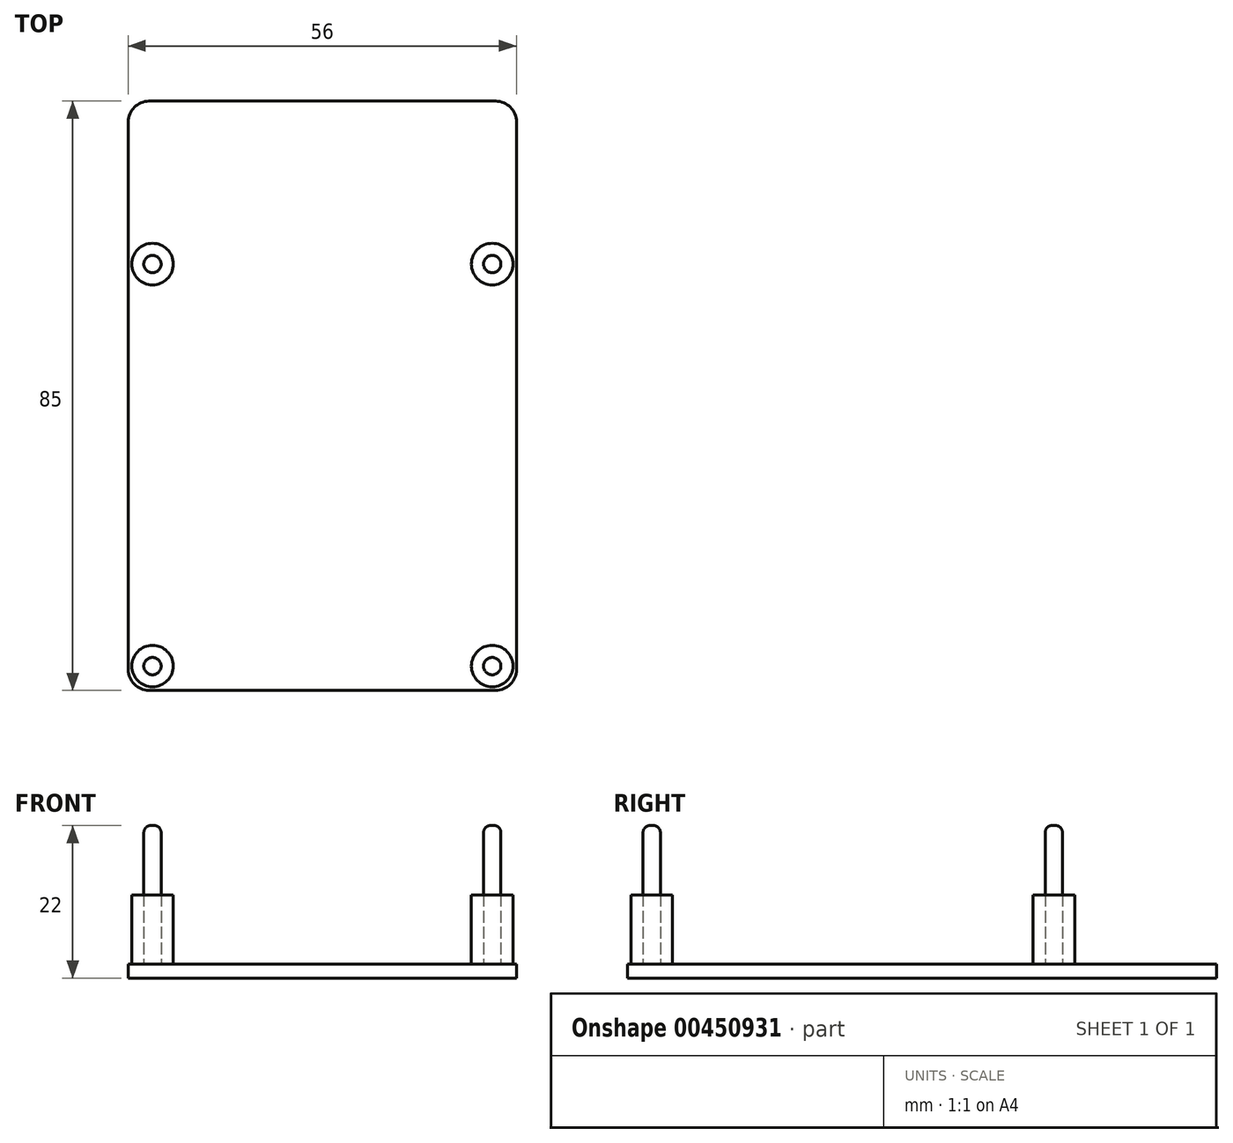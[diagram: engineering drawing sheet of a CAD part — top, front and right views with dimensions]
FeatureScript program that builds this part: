
annotation { "Feature Type Name" : "Feature", "Feature Type Description" : "" }
export const myFeature = defineFeature(function(context is Context, id is Id, definition is map)
    precondition{}
    {
        {
            var Q0;
            Q0=qCreatedBy(makeId("Top.planeOp"),FACE);
            var sketch = newSketch(context, id + "F0", { "sketchPlane" : qUnion([Q0])});
            skLineSegment(sketch, "E0.bottom", {"start": v(28, -42.5) * mm, "end": v(-28, -42.5) * mm});
            skLineSegment(sketch, "E0.top", {"start": v(28, 42.5) * mm, "end": v(-28, 42.5) * mm});
            skLineSegment(sketch, "E0.left", {"start": v(28, -42.5) * mm, "end": v(28, 42.5) * mm});
            skLineSegment(sketch, "E0.right", {"start": v(-28, -42.5) * mm, "end": v(-28, 42.5) * mm});
            skPoint(sketch, "E0.middle", {"position": v(0, 0) * mm});
            skSolve(sketch);
        }
        {
            var Q0;
            Q0=qSketchRegion(id+"F0",true);
            extrude(context, id + "F1", {"entities" : qUnion([Q0]), "depth" : 2 * mm, "offsetDistance" : 25 * mm});
        }
        {
            var Q0;
            Q0=makeQuery(id+"F1.opExtrude","SWEPT_EDGE",EDGE,{"disambiguationData":[OSD([sQuery(id+"F0.wireOp",EDGE,"E0.top"),sQuery(id+"F0.wireOp",EDGE,"E0.right")])]});
            var Q1;
            Q1=makeQuery(id+"F1.opExtrude","SWEPT_EDGE",EDGE,{"disambiguationData":[OSD([sQuery(id+"F0.wireOp",EDGE,"E0.top"),sQuery(id+"F0.wireOp",EDGE,"E0.left")])]});
            var Q2;
            Q2=makeQuery(id+"F1.opExtrude","SWEPT_EDGE",EDGE,{"disambiguationData":[OSD([sQuery(id+"F0.wireOp",EDGE,"E0.bottom"),sQuery(id+"F0.wireOp",EDGE,"E0.left")])]});
            var Q3;
            Q3=makeQuery(id+"F1.opExtrude","SWEPT_EDGE",EDGE,{"disambiguationData":[OSD([sQuery(id+"F0.wireOp",EDGE,"E0.bottom"),sQuery(id+"F0.wireOp",EDGE,"E0.right")])]});
            fillet(context, id + "F2", {"entities" : qUnion([Q0, Q1, Q2, Q3]), "radius" : 3 * mm, "tangentPropagation" : true, "allowEdgeOverflow" : false});
        }
        {
            var Q0;
            Q0=makeQuery(id+"F1.opExtrude","CAP_FACE",FACE,{"disambiguationData":[OSD([sQuery(id+"F0.wireOp",EDGE,"E0.bottom"),sQuery(id+"F0.wireOp",EDGE,"E0.top"),sQuery(id+"F0.wireOp",EDGE,"E0.left"),sQuery(id+"F0.wireOp",EDGE,"E0.right")])],"isStart":false});
            var sketch = newSketch(context, id + "F3", { "sketchPlane" : qUnion([Q0])});
            skCircle(sketch, "E1", {"center": v(-24.5, -39) * mm, "radius": 1.25 * mm});
            skCircle(sketch, "E2", {"center": v(24.5, -39) * mm, "radius": 1.25 * mm});
            skCircle(sketch, "E3", {"center": v(-24.5, 19) * mm, "radius": 1.25 * mm});
            skCircle(sketch, "E4", {"center": v(24.5, 19) * mm, "radius": 1.25 * mm});
            skSolve(sketch);
        }
        {
            var Q0;
            Q0=makeQuery(id+"F3.imprint","IMPRINT",FACE,{"disambiguationData":[TD([[makeQuery(id+"F3.imprint","IMPRINT",EDGE,{"derivedFrom":sQuery(id+"F3.wireOp",EDGE,"E1")}),-1.0]])]});
            var sketch = newSketch(context, id + "F4", { "sketchPlane" : qUnion([Q0])});
            skCircle(sketch, "E5", {"center": v(-24.5, 19) * mm, "radius": 3 * mm});
            skCircle(sketch, "E6", {"center": v(24.5, 19) * mm, "radius": 3 * mm});
            skCircle(sketch, "E7", {"center": v(-24.5, -39) * mm, "radius": 3 * mm});
            skCircle(sketch, "E8", {"center": v(24.5, -39) * mm, "radius": 3 * mm});
            skSolve(sketch);
        }
        {
            var Q0;
            Q0=qSketchRegion(id+"F3",true);
            extrude(context, id + "F5", {"entities" : qUnion([Q0]), "depth" : 20 * mm, "offsetDistance" : 25 * mm});
        }
        {
            var Q0;
            Q0=qSketchRegion(id+"F4",true);
            extrude(context, id + "F6", {"entities" : qUnion([Q0]), "depth" : 10 * mm, "offsetDistance" : 25 * mm});
        }
        {
            var Q0;
            Q0=makeQuery(id+"F5.opExtrude","CAP_EDGE",EDGE,{"disambiguationData":[OSD([sQuery(id+"F3.wireOp",EDGE,"E3")])],"isStart":false});
            var Q1;
            Q1=makeQuery(id+"F5.opExtrude","CAP_EDGE",EDGE,{"disambiguationData":[OSD([sQuery(id+"F3.wireOp",EDGE,"E1")])],"isStart":false});
            var Q2;
            Q2=makeQuery(id+"F5.opExtrude","CAP_EDGE",EDGE,{"disambiguationData":[OSD([sQuery(id+"F3.wireOp",EDGE,"E2")])],"isStart":false});
            var Q3;
            Q3=makeQuery(id+"F5.opExtrude","CAP_EDGE",EDGE,{"disambiguationData":[OSD([sQuery(id+"F3.wireOp",EDGE,"E4")])],"isStart":false});
            fillet(context, id + "F7", {"entities" : qUnion([Q0, Q1, Q2, Q3]), "radius" : 1 * mm, "tangentPropagation" : true, "allowEdgeOverflow" : false});
        }
    });
